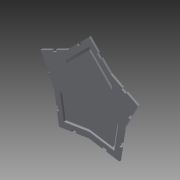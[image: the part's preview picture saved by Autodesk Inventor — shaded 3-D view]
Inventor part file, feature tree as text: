
AUTODESK INVENTOR PART (.ipt)
format: ipt  version: 2015 (Build 190159000, 159)  size: 211,968 bytes
history: native  units: in
note: dims shown in document units (in); Inventor stores cm internally (conversion verified against a paired STEP export)
features: sketch x4, extrude x3, other x2
ambient origin geometry x8: Origin, YZ Plane, XZ Plane, XY Plane, X Axis, Y Axis, Z Axis, Center Point
bodies: Solid1 (feature_tree)
feature tree (9):
  extrude  "Extrusion1"  Depth=7.0in
  extrude  "Extrusion2"  Depth=1.9685in TaperAngle=360.0deg
  sketch  "Sketch3"  dims[d10=0.125in d11=0.0in d12=0.15in]
  other  "Work Axis1"
  other  "Work Axis2"
  extrude  "Extrusion3"  Depth=0.15in
  sketch  "Sketch1"  dims[d0=5.0in d1=7.0in]
  sketch  "Sketch2"  dims[d2=1.9685in d4=360.0deg d6=1.9685in d8=360.0deg]
  sketch  "Sketch4"  dims[d13=0.15in d14=0.125in d15=0.15in d16=0.3in d18=0.15in d20=1.0in d21=0.0in d22=3.5in d23=7.1937in d24=0.15in d26=0.4in d27=0.4in d29=0.15in d30=0.1in d32=0.1in d33=0.15in d34=0.15in d35=0.15in d36=0.15in d37=0.4in d38=0.4in d39=0.4in d40=0.4in d44=45.0deg d45=45.0deg d46=45.0deg d47=45.0deg d48=0.1in d50=0.1in d51=1.0in d52=0.0in]
